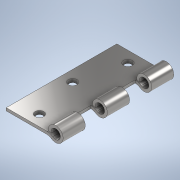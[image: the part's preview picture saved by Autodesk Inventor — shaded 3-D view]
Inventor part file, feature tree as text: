
AUTODESK INVENTOR PART (.ipt)
format: ipt  version: 2021 (Build 250183000, 183)  size: 174,592 bytes
history: native  units: mm
features: extrude x3, sketch x3
ambient origin geometry x8: Origin, YZ Plane, XZ Plane, XY Plane, X Axis, Y Axis, Z Axis, Center Point
bodies: Solid1 (feature_tree)
feature tree (6):
  extrude  "Extrusion1"  Depth=2.5mm
  extrude  "Extrusion2"  Depth=100.0mm TaperAngle=0.0deg
  extrude  "Extrusion3"  Depth=100.0mm
  sketch  "Sketch1"  dims[d1=2.5mm d2=2.5mm]
  sketch  "Sketch2"  dims[d3=8.5mm d4=100.0mm d5=0.0mm]
  sketch  "Sketch4"  dims[d6=8.0mm d7=8.0mm d8=8.0mm d9=10.0mm d10=20.0mm d11=20.0mm d12=10.0mm d13=10.0mm d14=50.0mm d15=100.0mm d16=-3.490659mm d22=20.0mm d23=20.0mm d24=20.0mm d25=20.0mm d26=100.0mm d27=0.0mm]
